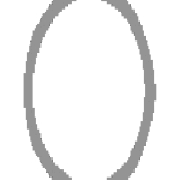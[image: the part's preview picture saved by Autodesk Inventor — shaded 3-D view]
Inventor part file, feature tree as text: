
AUTODESK INVENTOR PART (.ipt)
format: ipt  version: 2021 (Build 250183000, 183)  size: 109,568 bytes
history: native  units: in
note: dims shown in document units (in); Inventor stores cm internally (conversion verified against a paired STEP export)
features: other x4, sketch x3, plane x1
ambient origin geometry x8: Origin, YZ Plane, XZ Plane, XY Plane, X Axis, Y Axis, Z Axis, Center Point
bodies: Solid1 (feature_tree), Body (feature_tree)
feature tree (8):
  other  "Driven Length"
  other  "Frame Generator"
  other  "Start Plane"
  other  "End Plane"
  sketch  "Sketch"  dims[d2=19.6468in d4=-0.0in d5=19.6468in d6=0.12in d7=0.0in d8=90.0deg d9=19.6468in]
  sketch  "Sketch2"  dims[d0=1.0in]
  plane  "Work Plane3"
  sketch  "Sketch3"  dims[d1=0.065in]
